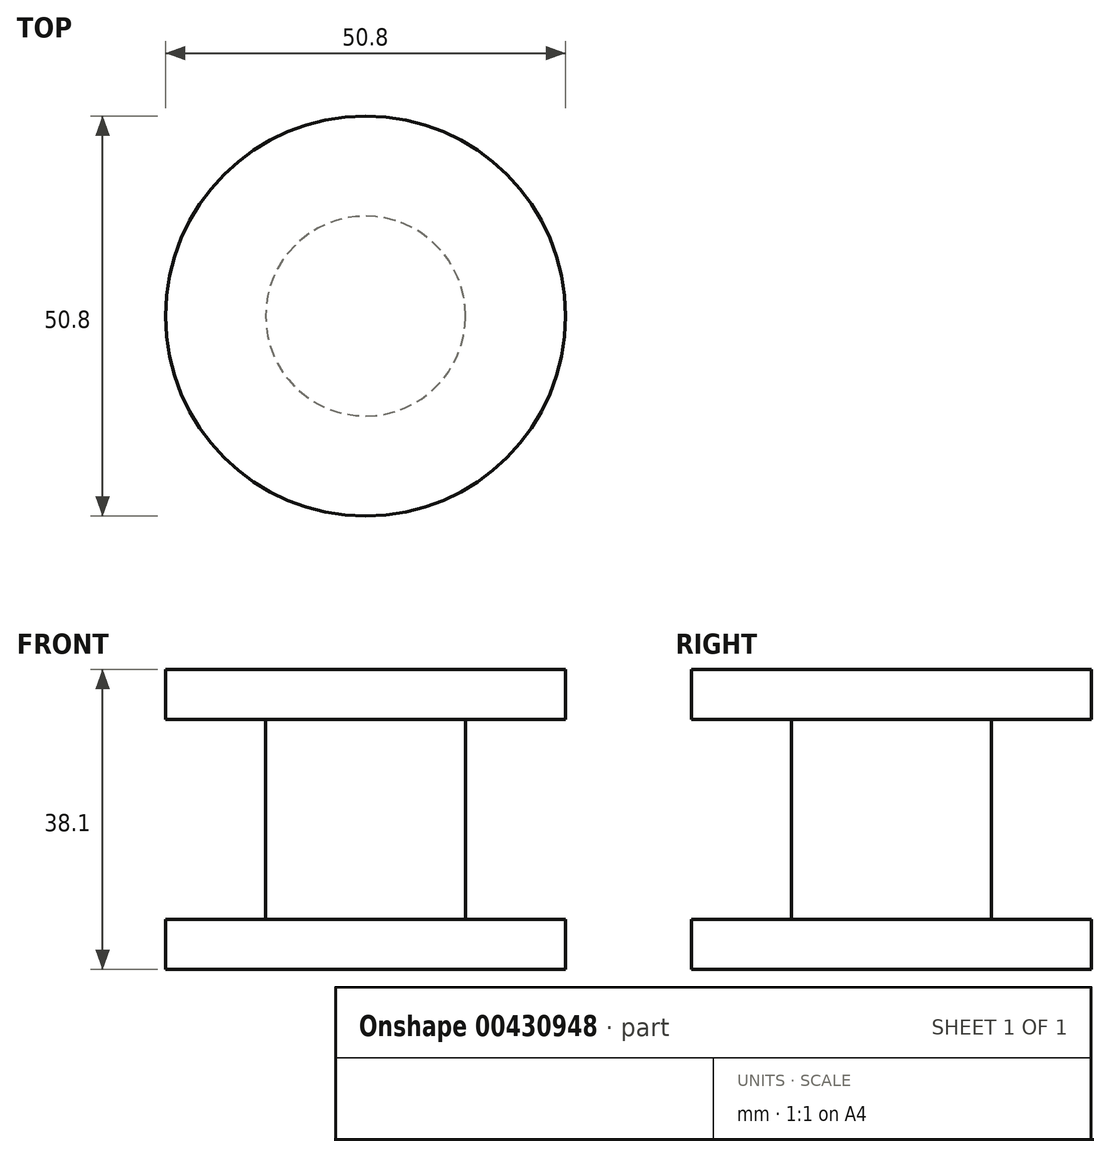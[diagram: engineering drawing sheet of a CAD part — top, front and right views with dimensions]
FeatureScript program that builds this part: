
annotation { "Feature Type Name" : "Feature", "Feature Type Description" : "" }
export const myFeature = defineFeature(function(context is Context, id is Id, definition is map)
    precondition{}
    {
        {
            var Q0;
            Q0=qCreatedBy(makeId("Front.planeOp"),FACE);
            var sketch = newSketch(context, id + "F0", { "sketchPlane" : qUnion([Q0])});
            skLineSegment(sketch, "E0", {"start": v(0, 19.05) * mm, "end": v(25.4, 19.05) * mm});
            skLineSegment(sketch, "E1", {"start": v(25.4, 19.05) * mm, "end": v(25.4, 12.7) * mm});
            skLineSegment(sketch, "E2", {"start": v(25.4, 12.7) * mm, "end": v(12.7, 12.7) * mm});
            skLineSegment(sketch, "E3", {"start": v(12.7, 12.7) * mm, "end": v(12.7, -12.7) * mm});
            skLineSegment(sketch, "E4", {"start": v(12.7, -12.7) * mm, "end": v(25.4, -12.7) * mm});
            skLineSegment(sketch, "E5", {"start": v(25.4, -12.7) * mm, "end": v(25.4, -19.05) * mm});
            skLineSegment(sketch, "E6", {"start": v(25.4, -19.05) * mm, "end": v(0, -19.05) * mm});
            skLineSegment(sketch, "E7", {"start": v(0, -19.05) * mm, "end": v(0, 19.05) * mm});
            skLineSegment(sketch, "E8", {"start": v(0, 39.4) * mm, "end": v(0, -42.82) * mm, "construction": true});
            skSolve(sketch);
        }
        {
            var Q0;
            Q0=makeQuery(id+"F0.imprint","IMPRINT",FACE,{"disambiguationData":[TD([[makeQuery(id+"F0.imprint","IMPRINT",EDGE,{"derivedFrom":sQuery(id+"F0.wireOp",EDGE,"E0")}),-1.0]])]});
            var Q1;
            Q1=sQuery(id+"F0.wireOp",EDGE,"E8");
            revolve(context, id + "F1", {"entities" : qUnion([Q0]), "axis" : qUnion([Q1]), "revolveType" : RevolveType.FULL});
        }
    });
